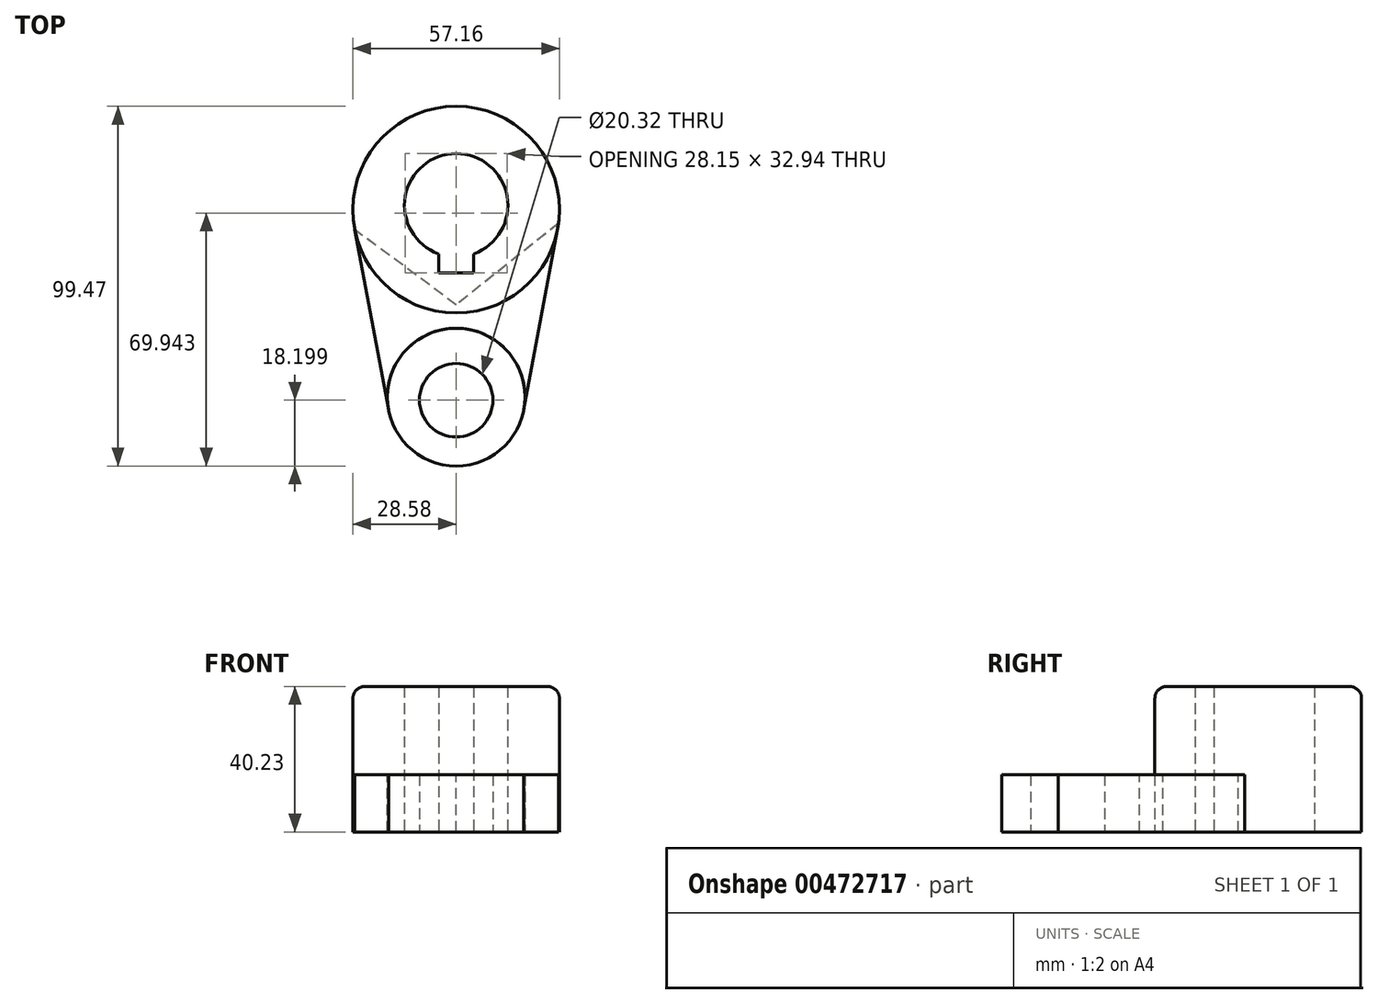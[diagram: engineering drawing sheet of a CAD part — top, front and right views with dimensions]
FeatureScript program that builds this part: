
annotation { "Feature Type Name" : "Feature", "Feature Type Description" : "" }
export const myFeature = defineFeature(function(context is Context, id is Id, definition is map)
    precondition{}
    {
        {
            var Q0;
            Q0=qCreatedBy(makeId("Top.planeOp"),FACE);
            var sketch = newSketch(context, id + "F0", { "sketchPlane" : qUnion([Q0])});
            skCircle(sketch, "E0", {"center": v(0, -26.37) * mm, "radius": 10.16 * mm});
            skSolve(sketch);
        }
        {
            var Q0;
            Q0=qCreatedBy(makeId("Top.planeOp"),FACE);
            var sketch = newSketch(context, id + "F1", { "sketchPlane" : qUnion([Q0])});
            skCircle(sketch, "E1", {"center": v(0, 27.55) * mm, "radius": 14.29 * mm});
            skSolve(sketch);
        }
        {
            var Q0;
            Q0=qCreatedBy(makeId("Top.planeOp"),FACE);
            var sketch = newSketch(context, id + "F2", { "sketchPlane" : qUnion([Q0])});
            skCircle(sketch, "E2", {"center": v(0, -25.52) * mm, "radius": 19.05 * mm});
            skSolve(sketch);
        }
        {
            var Q0;
            Q0=qCreatedBy(makeId("Top.planeOp"),FACE);
            var sketch = newSketch(context, id + "F3", { "sketchPlane" : qUnion([Q0])});
            skCircle(sketch, "E3", {"center": v(0, 26.33) * mm, "radius": 28.58 * mm});
            skSolve(sketch);
        }
        {
            var Q0;
            Q0=makeQuery(id+"F3.imprint","IMPRINT",FACE,{"disambiguationData":[TD([[makeQuery(id+"F3.imprint","IMPRINT",EDGE,{"derivedFrom":sQuery(id+"F3.wireOp",EDGE,"E3")}),1.0]])]});
            extrude(context, id + "F4", {"entities" : qUnion([Q0]), "depth" : 40.23 * mm});
        }
        {
            var Q0;
            Q0=makeQuery(id+"F2.imprint","IMPRINT",FACE,{"disambiguationData":[TD([[makeQuery(id+"F2.imprint","IMPRINT",EDGE,{"derivedFrom":sQuery(id+"F2.wireOp",EDGE,"E2")}),1.0]])]});
            extrude(context, id + "F5", {"entities" : qUnion([Q0]), "depth" : 15.77 * mm});
        }
        {
            var Q0;
            Q0=makeQuery(id+"F1.imprint","IMPRINT",FACE,{"disambiguationData":[TD([[makeQuery(id+"F1.imprint","IMPRINT",EDGE,{"derivedFrom":sQuery(id+"F1.wireOp",EDGE,"E1")}),1.0]])]});
            extrude(context, id + "F6", {"entities" : qUnion([Q0]), "operationType" : NewBodyOperationType.REMOVE, "depth" : 63.75 * mm});
        }
        {
            var Q0;
            Q0=makeQuery(id+"F4.opExtrude","CAP_FACE",FACE,{"disambiguationData":[OSD([sQuery(id+"F3.wireOp",EDGE,"E3")])],"isStart":true});
            var sketch = newSketch(context, id + "F7", { "sketchPlane" : qUnion([Q0])});
            skLineSegment(sketch, "E4.bottom", {"start": v(-4.84, -8.9) * mm, "end": v(4.84, -8.9) * mm});
            skLineSegment(sketch, "E4.top", {"start": v(-4.84, -17.63) * mm, "end": v(4.84, -17.63) * mm});
            skLineSegment(sketch, "E4.left", {"start": v(-4.84, -8.9) * mm, "end": v(-4.84, -17.63) * mm});
            skLineSegment(sketch, "E4.right", {"start": v(4.84, -8.9) * mm, "end": v(4.84, -17.63) * mm});
            skPoint(sketch, "E4.middle", {"position": v(0, -13.27) * mm});
            skLineSegment(sketch, "E5.bottom", {"start": v(-3.37, -9.82) * mm, "end": v(-6.3, -9.82) * mm, "construction": true});
            skLineSegment(sketch, "E5.top", {"start": v(-3.37, -7.99) * mm, "end": v(-6.3, -7.99) * mm, "construction": true});
            skLineSegment(sketch, "E5.left", {"start": v(-3.37, -9.82) * mm, "end": v(-3.37, -7.99) * mm, "construction": true});
            skLineSegment(sketch, "E5.right", {"start": v(-6.3, -9.82) * mm, "end": v(-6.3, -7.99) * mm, "construction": true});
            skPoint(sketch, "E5.middle", {"position": v(-4.84, -8.9) * mm});
            skSolve(sketch);
        }
        {
            var Q0;
            Q0=makeQuery(id+"F0.imprint","IMPRINT",FACE,{"disambiguationData":[TD([[makeQuery(id+"F0.imprint","IMPRINT",EDGE,{"derivedFrom":sQuery(id+"F0.wireOp",EDGE,"E0")}),1.0]])]});
            extrude(context, id + "F8", {"entities" : qUnion([Q0]), "operationType" : NewBodyOperationType.REMOVE, "depth" : 111.5 * mm});
        }
        {
            var Q0;
            Q0=makeQuery(id+"F4.opExtrude","CAP_EDGE",EDGE,{"disambiguationData":[OSD([sQuery(id+"F3.wireOp",EDGE,"E3")])],"isStart":false});
            fillet(context, id + "F9", {"entities" : qUnion([Q0]), "radius" : 3.3 * mm, "tangentPropagation" : true, "allowEdgeOverflow" : false});
        }
        {
            var Q0;
            Q0=makeQuery(id+"F5.opExtrude","CAP_FACE",FACE,{"disambiguationData":[OSD([sQuery(id+"F2.wireOp",EDGE,"E2")])],"isStart":false});
            var sketch = newSketch(context, id + "F10", { "sketchPlane" : qUnion([Q0])});
            skLineSegment(sketch, "E6", {"start": v(-18.73, -29.02) * mm, "end": v(-28.04, 20.8) * mm});
            skLineSegment(sketch, "E7", {"start": v(18.73, -29.02) * mm, "end": v(28.37, 22.6) * mm});
            skLineSegment(sketch, "E8", {"start": v(28.37, 22.6) * mm, "end": v(0, 0) * mm});
            skLineSegment(sketch, "E9", {"start": v(0, 0) * mm, "end": v(-28.04, 20.8) * mm});
            skLineSegment(sketch, "E10", {"start": v(-18.73, -29.02) * mm, "end": v(-2.14, -8.02) * mm});
            skLineSegment(sketch, "E11", {"start": v(-2.14, -8.02) * mm, "end": v(18.73, -29.02) * mm});
            skSolve(sketch);
        }
        {
            var Q0;
            {var subQ1=sQuery(id+"F10.wireOp",EDGE,"E6");Q0=makeQuery(id+"F10.imprint","IMPRINT",FACE,{"disambiguationData":[TD([[makeQuery(id+"F10.imprint","IMPRINT",EDGE,{"derivedFrom":subQ1}),-1.0]])]});}
            extrude(context, id + "F11", {"entities" : qUnion([Q0]), "oppositeDirection" : true, "depth" : 15.77 * mm});
        }
        {
            var Q0;
            {var subQ0=sQuery(id+"F7.wireOp",EDGE,"E4.bottom");Q0=makeQuery(id+"F7.imprint","IMPRINT",FACE,{"disambiguationData":[TD([[makeQuery(id+"F7.imprint","IMPRINT",EDGE,{"derivedFrom":subQ0}),-1.0]])]});}
            extrude(context, id + "F12", {"entities" : qUnion([Q0]), "operationType" : NewBodyOperationType.REMOVE, "oppositeDirection" : true, "depth" : 175.5 * mm});
        }
    });
